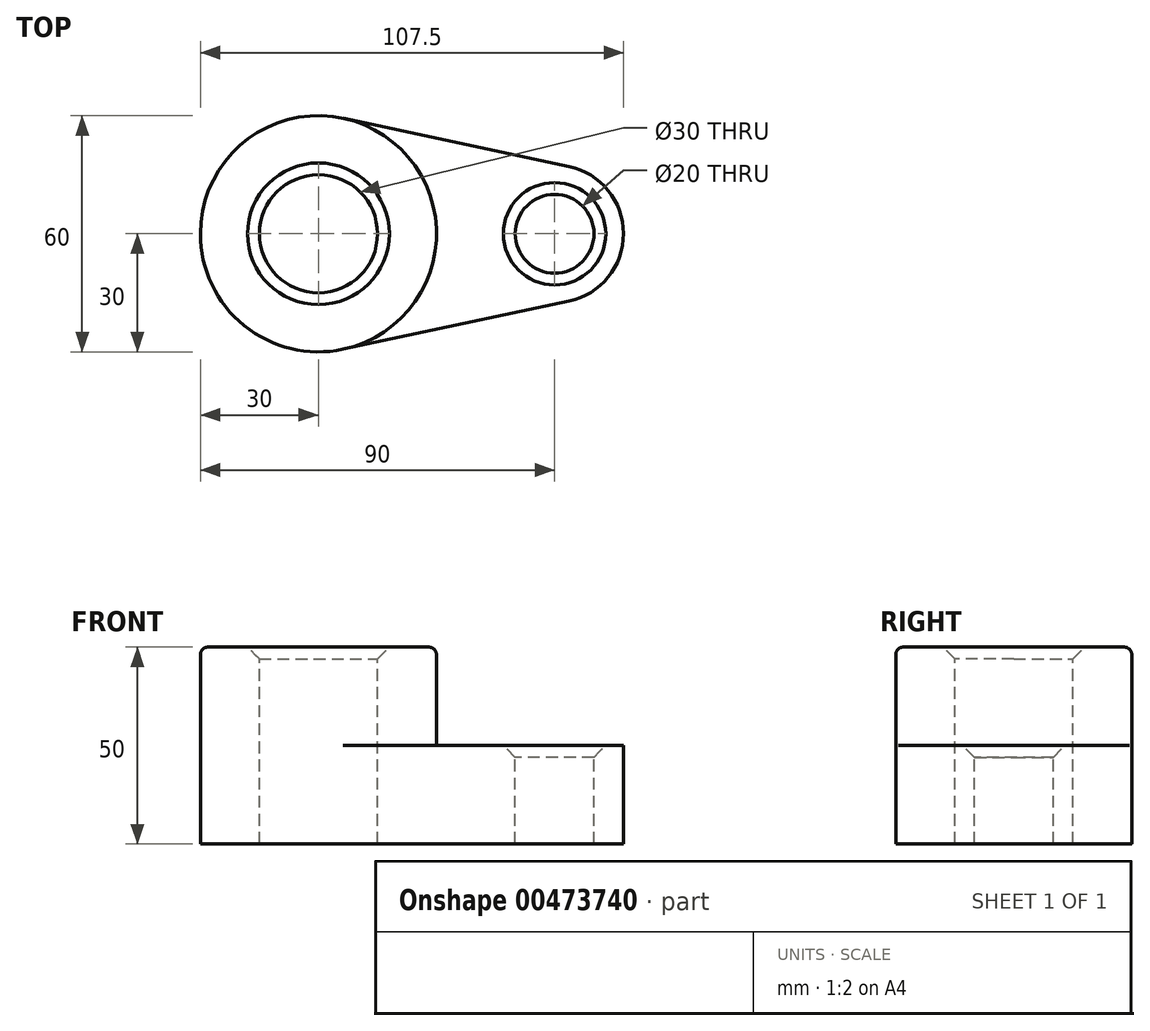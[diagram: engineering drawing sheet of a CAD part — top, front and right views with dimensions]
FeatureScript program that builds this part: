
annotation { "Feature Type Name" : "Feature", "Feature Type Description" : "" }
export const myFeature = defineFeature(function(context is Context, id is Id, definition is map)
    precondition{}
    {
        {
            var Q0;
            Q0=qCreatedBy(makeId("Top.planeOp"),FACE);
            var sketch = newSketch(context, id + "F0", { "sketchPlane" : qUnion([Q0])});
            skCircle(sketch, "E0", {"center": v(0, 0) * mm, "radius": 30 * mm});
            skCircle(sketch, "E1", {"center": v(60, 0) * mm, "radius": 17.5 * mm});
            skLineSegment(sketch, "E2", {"start": v(6.25, -29.34) * mm, "end": v(63.65, -17.12) * mm});
            skLineSegment(sketch, "E3", {"start": v(6.25, 29.34) * mm, "end": v(63.65, 17.12) * mm});
            skCircle(sketch, "E4", {"center": v(0, 0) * mm, "radius": 15 * mm});
            skCircle(sketch, "E5", {"center": v(60, 0) * mm, "radius": 10 * mm});
            skSolve(sketch);
        }
        {
            var Q0;
            Q0 = qSketchRegion(id + "F0", true);
            extrude(context, id + "F1", {"entities" : qUnion([Q0]), "oppositeDirection" : true, "depth" : 25 * mm});
        }
        {
            var Q0;
            Q0=makeQuery(id+"F1.opExtrude","CAP_FACE",FACE,{"disambiguationData":[OSD([sQuery(id+"F0.wireOp",EDGE,"E0"),sQuery(id+"F0.wireOp",EDGE,"E1"),sQuery(id+"F0.wireOp",EDGE,"E2"),sQuery(id+"F0.wireOp",EDGE,"E3"),sQuery(id+"F0.wireOp",EDGE,"E4"),sQuery(id+"F0.wireOp",EDGE,"E5")])],"isStart":false});
            var sketch = newSketch(context, id + "F2", { "sketchPlane" : qUnion([Q0])});
            skCircle(sketch, "E6", {"center": v(0, 0) * mm, "radius": 30 * mm});
            skSolve(sketch);
        }
        {
            var Q0;
            {var subQ0=sQuery(id+"F2.wireOp",EDGE,"E6");Q0=makeQuery(id+"F2.imprint","IMPRINT",FACE,{"disambiguationData":[TD([[makeQuery(id+"F2.imprint","IMPRINT",EDGE,{"disambiguationData":[OD(0.0)],"derivedFrom":subQ0}),-1.0]])]});}
            extrude(context, id + "F3", {"entities" : qUnion([Q0]), "operationType" : NewBodyOperationType.ADD, "oppositeDirection" : true, "depth" : 50 * mm});
        }
        {
            var Q0;
            Q0=makeQuery(id+"F3.opExtrude","CAP_EDGE",EDGE,{"disambiguationData":[OSD([sQuery(id+"F2.wireOp",EDGE,"E6")])],"isStart":false});
            fillet(context, id + "F4", {"entities" : qUnion([Q0]), "radius" : 2 * mm, "tangentPropagation" : true, "allowEdgeOverflow" : false});
        }
        {
            var Q0;
            Q0=makeQuery(id+"F3.opExtrude","CAP_EDGE",EDGE,{"disambiguationData":[OSD([sQuery(id+"F0.wireOp",EDGE,"E4")])],"isStart":false});
            var Q1;
            Q1=makeQuery(id+"F1.opExtrude","CAP_EDGE",EDGE,{"disambiguationData":[OSD([sQuery(id+"F0.wireOp",EDGE,"E5")])],"isStart":true});
            chamfer(context, id + "F5", {"entities" : qUnion([Q0, Q1]), "width" : 3 * mm, "tangentPropagation" : true});
        }
    });
